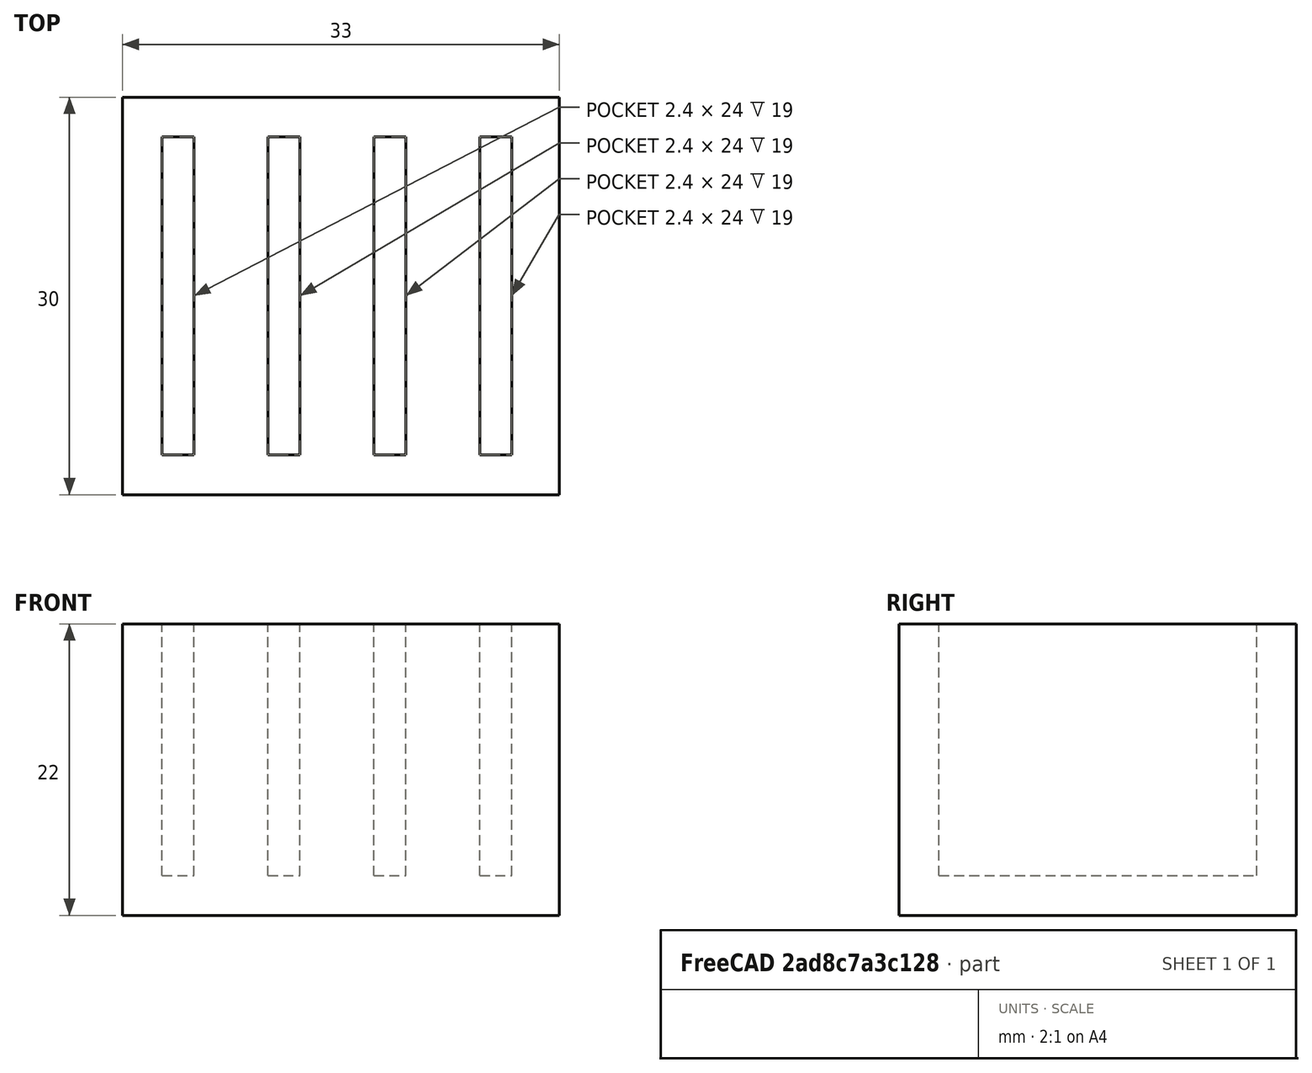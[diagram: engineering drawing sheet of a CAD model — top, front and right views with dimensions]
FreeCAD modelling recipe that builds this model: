
FCSTD DOCUMENT  (FreeCAD 0.21R33771 (Git))
Label: OJT1_T08R01_portasds
License: All rights reserved
LicenseURL: http://en.wikipedia.org/wiki/All_rights_reserved
objects: Part::Box×5, Part::MultiFuse×1, Part::Cut×1
note: 7 computed .brp shape members not serialized (recipe doc carries the construction recipe); baked Part::Feature solids carry a one-line shape summary decoded from their .brp

FEATURE [Part::Box] Box  label="ranura1"
  AttacherType = Attacher::AttachEngine3D
  Height = 22
  Length = 2.4
  Placement = pos=(3,3,3) rot=(0,0,1;0rad)
  Width = 24
FEATURE [Part::Box] Box001  label="ranura002"
  AttacherType = Attacher::AttachEngine3D
  Height = 22
  Length = 2.4
  Placement = pos=(11,3,3) rot=(0,0,1;0rad)
  Width = 24
FEATURE [Part::Box] Box002  label="ranura003"
  AttacherType = Attacher::AttachEngine3D
  Height = 22
  Length = 2.4
  Placement = pos=(19,3,3) rot=(0,0,1;0rad)
  Width = 24
FEATURE [Part::Box] Box003  label="ranura004"
  AttacherType = Attacher::AttachEngine3D
  Height = 22
  Length = 2.4
  Placement = pos=(27,3,3) rot=(0,0,1;0rad)
  Width = 24
FEATURE [Part::Box] Box004  label="base"
  AttacherType = Attacher::AttachEngine3D
  Height = 22
  Length = 33
  Width = 30
FEATURE [Part::MultiFuse] Fusion  label="ranures"
  Refine = true
  Shapes = -> [Box,Box001,Box002,Box003]
FEATURE [Part::Cut] Cut  label="portasds"
  Base = -> Box004
  Refine = true
  Tool = -> Fusion
